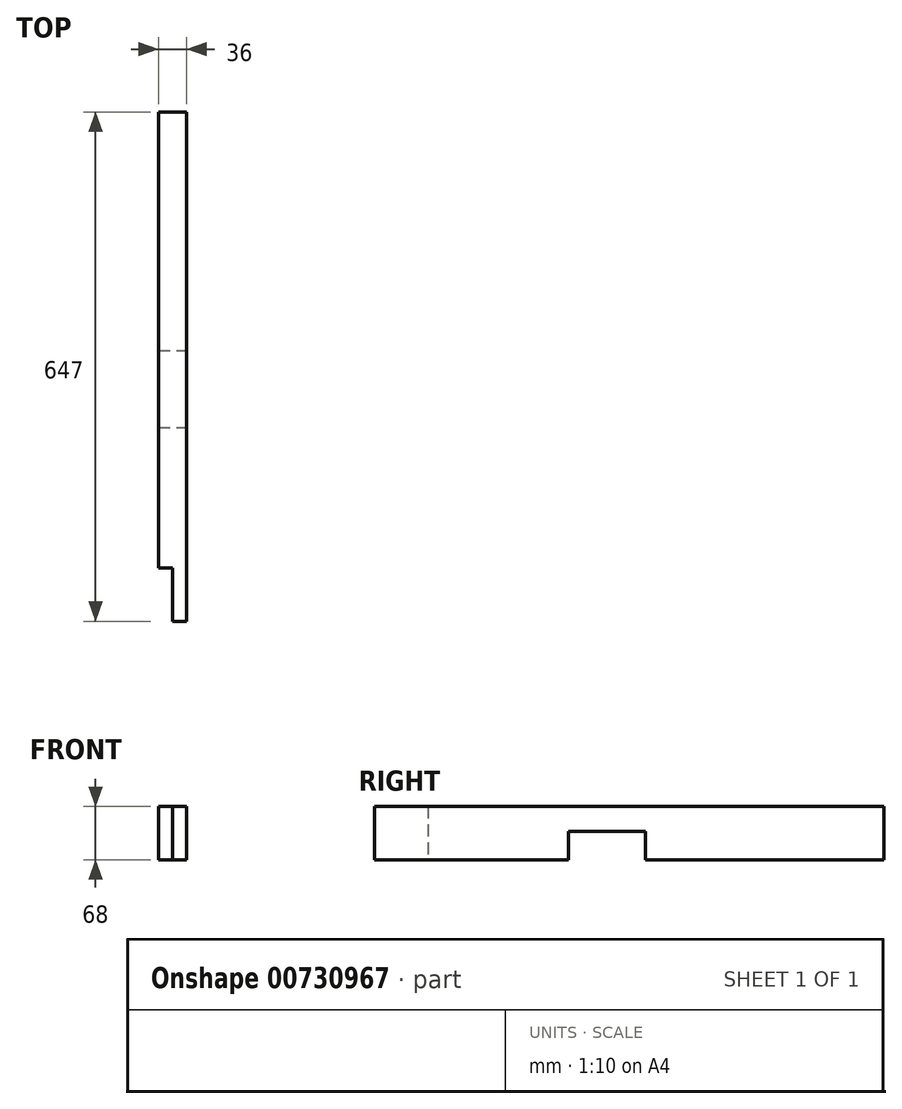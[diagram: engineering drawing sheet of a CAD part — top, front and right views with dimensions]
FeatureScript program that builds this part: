
annotation { "Feature Type Name" : "Feature", "Feature Type Description" : "" }
export const myFeature = defineFeature(function(context is Context, id is Id, definition is map)
    precondition{}
    {
        {
            var Q0;
            Q0=qCreatedBy(makeId("Front.planeOp"),FACE);
            var sketch = newSketch(context, id + "F0", { "sketchPlane" : qUnion([Q0])});
            skLineSegment(sketch, "E0.bottom", {"start": v(18, -34) * mm, "end": v(-18, -34) * mm});
            skLineSegment(sketch, "E0.top", {"start": v(18, 34) * mm, "end": v(-18, 34) * mm});
            skLineSegment(sketch, "E0.left", {"start": v(18, -34) * mm, "end": v(18, 34) * mm});
            skLineSegment(sketch, "E0.right", {"start": v(-18, -34) * mm, "end": v(-18, 34) * mm});
            skPoint(sketch, "E0.middle", {"position": v(0, 0) * mm});
            skSolve(sketch);
        }
        {
            var Q0;
            Q0=makeQuery(id+"F0.imprint","IMPRINT",FACE,{"disambiguationData":[TD([[makeQuery(id+"F0.imprint","IMPRINT",EDGE,{"derivedFrom":sQuery(id+"F0.wireOp",EDGE,"E0.bottom")}),-1.0]])]});
            extrude(context, id + "F1", {"entities" : qUnion([Q0]), "depth" : 647 * mm, "offsetDistance" : 25 * mm});
        }
        {
            var Q0;
            Q0=makeQuery(id+"F1.opExtrude","SWEPT_FACE",FACE,{"disambiguationData":[OSD([sQuery(id+"F0.wireOp",EDGE,"E0.left")])]});
            var sketch = newSketch(context, id + "F2", { "sketchPlane" : qUnion([Q0])});
            skLineSegment(sketch, "E1.bottom", {"start": v(-401, -34) * mm, "end": v(-303, -34) * mm});
            skLineSegment(sketch, "E1.top", {"start": v(-401, 2) * mm, "end": v(-303, 2) * mm});
            skLineSegment(sketch, "E1.left", {"start": v(-401, -34) * mm, "end": v(-401, 2) * mm});
            skLineSegment(sketch, "E1.right", {"start": v(-303, -34) * mm, "end": v(-303, 2) * mm});
            skSolve(sketch);
        }
        {
            var Q0;
            Q0=makeQuery(id+"F2.imprint","IMPRINT",FACE,{"disambiguationData":[TD([[makeQuery(id+"F2.imprint","IMPRINT",EDGE,{"derivedFrom":sQuery(id+"F2.wireOp",EDGE,"E1.bottom")}),1.0]])]});
            extrude(context, id + "F3", {"entities" : qUnion([Q0]), "operationType" : NewBodyOperationType.REMOVE, "endBound" : BoundingType.UP_TO_NEXT, "oppositeDirection" : true, "depth" : 25 * mm, "offsetDistance" : 25 * mm});
        }
        {
            var Q0;
            Q0=makeQuery(id+"F1.opExtrude","SWEPT_FACE",FACE,{"disambiguationData":[OSD([sQuery(id+"F0.wireOp",EDGE,"E0.right")])]});
            var sketch = newSketch(context, id + "F4", { "sketchPlane" : qUnion([Q0])});
            skSolve(sketch);
        }
        {
            var Q0;
            {var subQ0=sQuery(id+"F0.wireOp",EDGE,"E0.right");Q0=makeQuery(id+"F4.imprint","IMPRINT",FACE,{"disambiguationData":[TD([[makeQuery(id+"F4.imprint","IMPRINT",EDGE,{"derivedFrom":makeQuery(id+"F1.opExtrude","CAP_EDGE",EDGE,{"disambiguationData":[OSD([subQ0])],"isStart":true})}),-1.0]])]});}
            var sketch = newSketch(context, id + "F5", { "sketchPlane" : qUnion([Q0])});
            skLineSegment(sketch, "E2.bottom", {"start": v(579, 34) * mm, "end": v(647, 34) * mm});
            skLineSegment(sketch, "E2.top", {"start": v(579, -34) * mm, "end": v(647, -34) * mm});
            skLineSegment(sketch, "E2.left", {"start": v(647, 34) * mm, "end": v(647, -34) * mm});
            skLineSegment(sketch, "E2.right", {"start": v(579, 34) * mm, "end": v(579, -34) * mm});
            skSolve(sketch);
        }
        {
            var Q0;
            Q0 = qSketchRegion(id + "F5", true);
            extrude(context, id + "F6", {"entities" : qUnion([Q0]), "operationType" : NewBodyOperationType.REMOVE, "oppositeDirection" : true, "depth" : 18 * mm, "offsetDistance" : 25 * mm});
        }
    });
